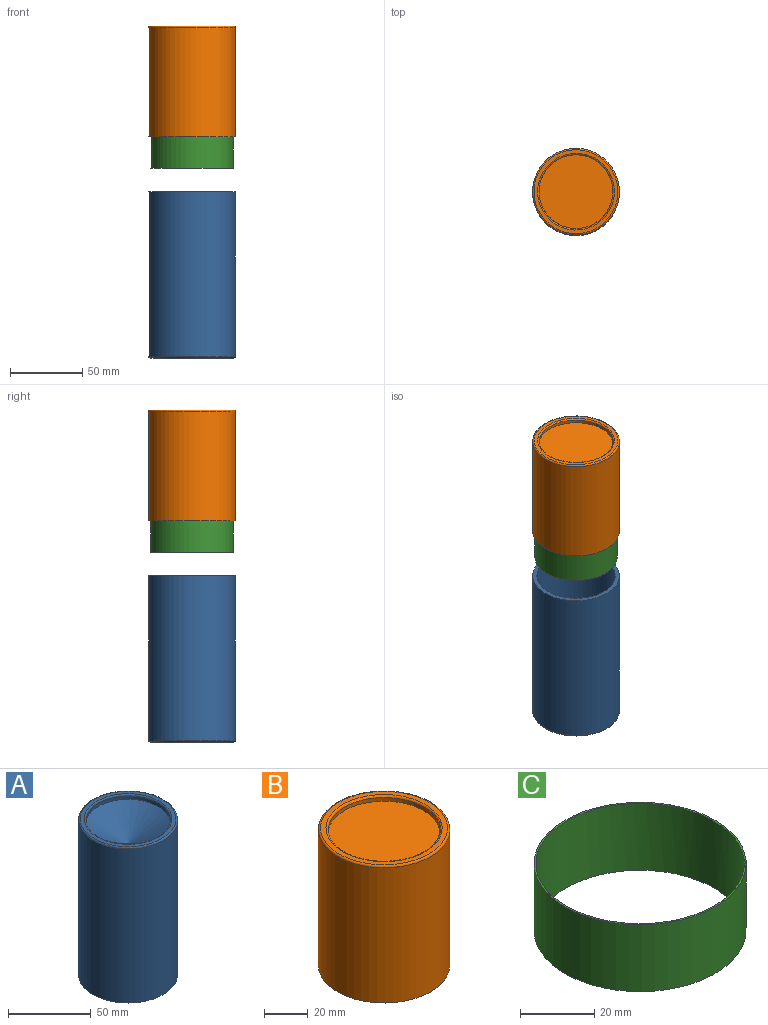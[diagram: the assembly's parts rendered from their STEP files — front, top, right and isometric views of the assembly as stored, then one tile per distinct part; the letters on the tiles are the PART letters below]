
ASSEMBLY  parts=3 mates=2
PART A: 9 faces, bbox 64.9x64.9x115 mm
  f0: cylinder r=30mm len=114mm, axis (0,0,-1), area 21488.5mm2, adj f2,f6
  f1: plane 58x58mm, normal (0,0,1), area 435.9mm2, adj f5,f6
  f2: plane 60x60mm, normal (0,0,-1), area 520.2mm2, adj f0,f7
  f3: cylinder r=25.5mm len=51mm, axis (0,0,1), area 400.6mm2, adj f4,f5
  f4: cone r=0mm half-angle=59deg, axis (0,0,1), area 2383.2mm2, adj f3
  f5: torus R=26.5mm, axis (0,0,1), area 255.3mm2, adj f1,f3
  f6: torus R=29mm, axis (0,0,1), area 292.5mm2, adj f0,f1
  f7: cylinder r=27.1mm len=109.08mm, axis (0,0,-1), area 18573.2mm2, adj f2,f8
  f8: cone r=1.49mm half-angle=59deg, axis (0,0,1), area 2691.7mm2, adj f7
PART B: 11 faces, bbox 64.9x64.9x76.5 mm
  f0: cylinder r=30mm len=75.5mm, axis (0,0,-1), area 14231.4mm2, adj f1,f6
  f1: plane 60x60mm, normal (0,0,-1), area 239.7mm2, adj f0,f7
  f2: plane 58x58mm, normal (0,0,1), area 435.9mm2, adj f5,f6
  f3: cylinder r=25.5mm len=51mm, axis (0,0,-1), area 320.4mm2, adj f4,f5
  f4: plane 51x51mm, normal (0,0,1), area 2042.8mm2, adj f3
  f5: torus R=26.5mm, axis (0,0,1), area 255.3mm2, adj f2,f3
  f6: torus R=29mm, axis (0,0,1), area 292.5mm2, adj f0,f2
  f7: cylinder r=28.7mm len=75.2mm, axis (0,0,-1), area 13560.6mm2, adj f1,f8
  f8: plane 57.4x57.4mm, normal (0,0,-1), area 331.3mm2, adj f7,f9
  f9: cylinder r=26.8mm len=53.6mm, axis (0,0,-1), area 505.2mm2, adj f8,f10
  f10: plane 53.6x53.6mm, normal (0,0,-1), area 2256.4mm2, adj f9
PART C: 4 faces, bbox 57x57x22 mm
  f0: cylinder r=28.5mm len=57mm, axis (0,0,-1), area 3939.6mm2, adj f1,f2
  f1: plane 57x57mm, normal (0,0,1), area 88.7mm2, adj f0,f3
  f2: plane 57x57mm, normal (0,0,-1), area 88.7mm2, adj f0,f3
  f3: cylinder r=28mm len=56mm, axis (0,0,-1), area 3870.4mm2, adj f1,f2
PLACE A rot(axis=(1,0,0),180deg) t=(-28.05,7.13,-41.26)mm
PLACE B t=(-28.05,7.13,-3.26)mm fixed
PLACE C t=(-28.05,7.13,-25.26)mm
MATE slider A.f0 <-> C.f0  axis (0,0,1) through (-28.05,7.13,-41.26)mm
MATE fastened B.f0 <-> C.f0  axis (0,0,-1) through (-28.05,7.13,-3.26)mm
